# Revit family: Sanitary_Bath-Spas_AXOR_38412USA-AXOR-Uno-Bath-spout-curved-floo_
name_source: partatom
category: Plumbing Fixtures
revit_build: Autodesk Revit 2018 (Build: 20170223_1515(x64)
units: mm (PartAtom-declared; Revit-internal decimal feet)

## family parameters
Always vertical = No
Cut with Voids When Loaded = No
OmniClass Number = 23.45.00.00
OmniClass Title = Sanitary, Laundry, and Cleaning Equipment
Part Type = Normal
Room Calculation Point = No
Round Connector Dimension = Use Diameter
Shared = No
Work Plane-Based = Yes

## types (4) — shared parameters
Always visible = Yes
BIMobject category = Bath & Spas
Default Elevation = 1219.2 mm  [stored 4 ft]
Design country = Germany
EAN code = 4059625075517
Edition number = 1
IFC Classification = Sanitary Terminal
Installation instructions = https://www.axor-design.com
Manufacturer country = Germany
Manufacturer name = AXOR
Material main = Chrome
Product Guid = c6511bc8-857d-4592-8e0e-b5a58b2398ff
Product SKU = 38412USA
Product data url = https://www.bimobject.com
Product family = AXOR Uno
Product group = Bath fillers
Product name = 38412USA AXOR Uno Bath spout curved floor-standing
Product url = https://www.axor-design.com
QR code = https://www.bimobject.com
Technical description = https://www.axor-design.com

## per-type parameters (varying)
| type | Material 1 |
| 331 Polished Black Chrome | AXOR - AXOR One - 331 Polished Black Chrome |
| 821 Brushed Nickel | AXOR - AXOR One - 821 Brushed Nickel |
| 141 Brushed Bronze | AXOR - AXOR One - 141 Brushed Bronze |
| 001 Chrome | AXOR - AXOR One - 001 Chrome |

note: [stored X ft] marks values corroborated as IEEE doubles in the binary element streams (Revit-internal decimal feet)

## geometry (parser evidence)
native form markers: Sweep x4
no freeform markers — native parametric forms only
